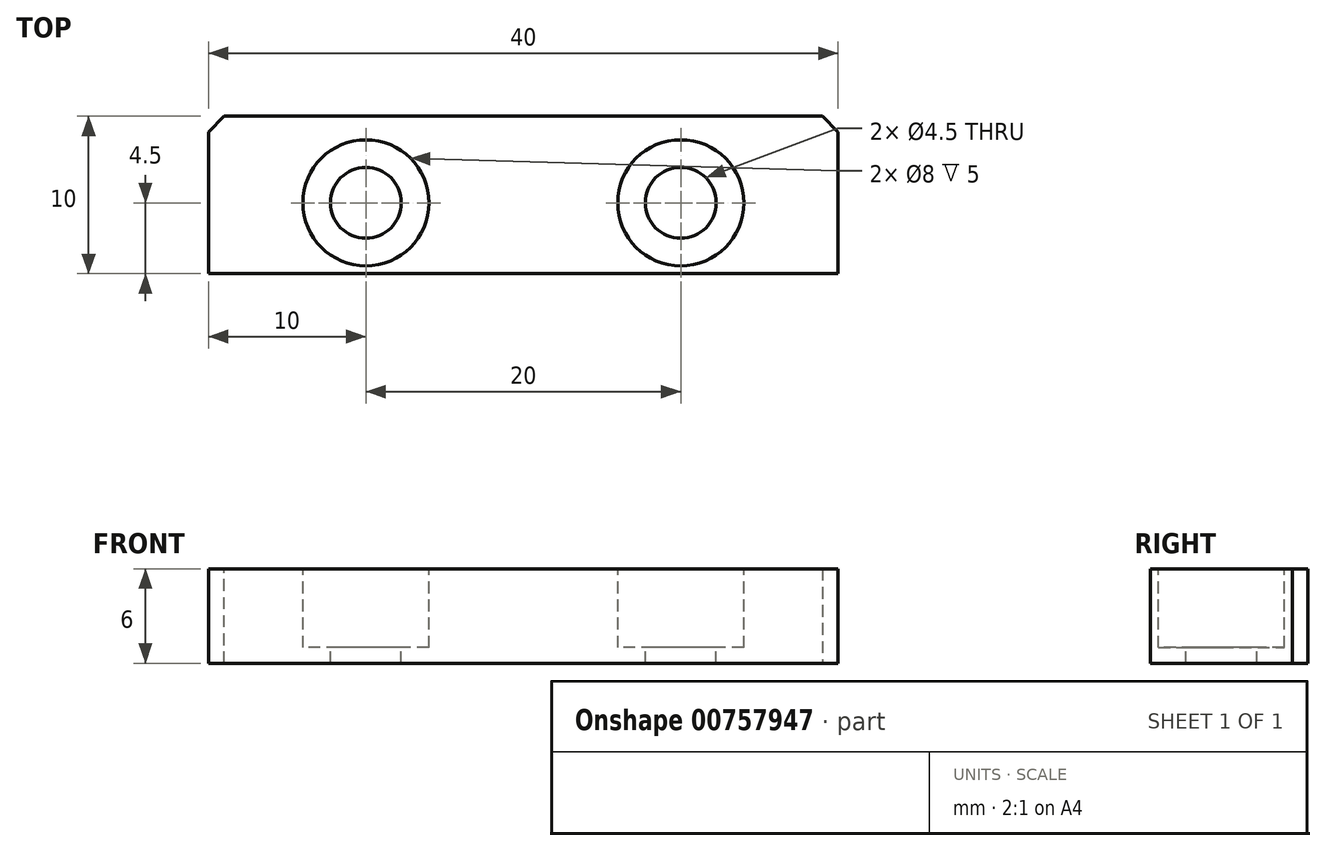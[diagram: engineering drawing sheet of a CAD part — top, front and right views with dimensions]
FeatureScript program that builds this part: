
annotation { "Feature Type Name" : "Feature", "Feature Type Description" : "" }
export const myFeature = defineFeature(function(context is Context, id is Id, definition is map)
    precondition{}
    {
        {
            var Q0;
            Q0=qCreatedBy(makeId("Top.planeOp"),FACE);
            var sketch = newSketch(context, id + "F0", { "sketchPlane" : qUnion([Q0])});
            skLineSegment(sketch, "E0.bottom", {"start": v(20, -5) * mm, "end": v(-20, -5) * mm});
            skLineSegment(sketch, "E0.top", {"start": v(20, 5) * mm, "end": v(-20, 5) * mm});
            skLineSegment(sketch, "E0.left", {"start": v(20, -5) * mm, "end": v(20, 5) * mm});
            skLineSegment(sketch, "E0.right", {"start": v(-20, -5) * mm, "end": v(-20, 5) * mm});
            skPoint(sketch, "E0.middle", {"position": v(0, 0) * mm});
            skSolve(sketch);
        }
        {
            var Q0;
            Q0=makeQuery(id+"F0.imprint","IMPRINT",FACE,{"disambiguationData":[TD([[makeQuery(id+"F0.imprint","IMPRINT",EDGE,{"derivedFrom":sQuery(id+"F0.wireOp",EDGE,"E0.bottom")}),-1.0]])]});
            extrude(context, id + "F1", {"entities" : qUnion([Q0]), "depth" : 6 * mm, "offsetDistance" : 25 * mm});
        }
        {
            var Q0;
            Q0=makeQuery(id+"F1.opExtrude","CAP_FACE",FACE,{"disambiguationData":[OSD([sQuery(id+"F0.wireOp",EDGE,"E0.bottom"),sQuery(id+"F0.wireOp",EDGE,"E0.top"),sQuery(id+"F0.wireOp",EDGE,"E0.left"),sQuery(id+"F0.wireOp",EDGE,"E0.right")])],"isStart":false});
            var sketch = newSketch(context, id + "F2", { "sketchPlane" : qUnion([Q0])});
            skPoint(sketch, "E1", {"position": v(-10, -0.5) * mm});
            skPoint(sketch, "E2.MirrorP", {"position": v(10, -0.5) * mm});
            skSolve(sketch);
        }
        {
            var Q0;
            Q0=sQuery(id+"F2.wireOp",VERTEX,"E1");
            var Q1;
            Q1=sQuery(id+"F2.wireOp",VERTEX,"E2.MirrorP");
            var Q2;
            Q2=makeQuery(id+"F1.opExtrude","SWEPT_BODY",BODY,{"disambiguationData":[OSD([sQuery(id+"F0.wireOp",EDGE,"E0.bottom"),sQuery(id+"F0.wireOp",EDGE,"E0.top"),sQuery(id+"F0.wireOp",EDGE,"E0.left"),sQuery(id+"F0.wireOp",EDGE,"E0.right")])]});
            hole(context, id + "F3", {"style" : HoleStyle.C_BORE, "endStyle" : HoleEndStyle.THROUGH, "holeDiameter" : 4.5 * mm, "cBoreDiameter" : 8 * mm, "cBoreDepth" : 5 * mm, "majorDiameter" : 5 * mm, "isTappedThrough" : true, "tappedDepth" : 6 * mm, "tapClearance" : 3, "locations" : qUnion([Q0, Q1]), "scope" : qUnion([Q2])});
        }
        {
            var Q0;
            Q0=makeQuery(id+"F1.opExtrude","SWEPT_EDGE",EDGE,{"disambiguationData":[OSD([sQuery(id+"F0.wireOp",EDGE,"E0.top"),sQuery(id+"F0.wireOp",EDGE,"E0.left")])]});
            var Q1;
            Q1=makeQuery(id+"F1.opExtrude","SWEPT_EDGE",EDGE,{"disambiguationData":[OSD([sQuery(id+"F0.wireOp",EDGE,"E0.top"),sQuery(id+"F0.wireOp",EDGE,"E0.right")])]});
            chamfer(context, id + "F4", {"entities" : qUnion([Q0, Q1]), "width" : 1 * mm, "tangentPropagation" : true});
        }
    });
